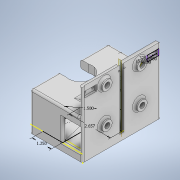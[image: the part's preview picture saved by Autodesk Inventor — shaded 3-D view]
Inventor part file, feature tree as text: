
AUTODESK INVENTOR PART (.ipt)
format: ipt  version: 2020 (Build 240168000, 168)  size: 502,784 bytes
history: native  units: in
note: dims shown in document units (in); Inventor stores cm internally (conversion verified against a paired STEP export)
features: sketch x18, extrude x14, hole x4, plane x1, mirror x1, fillet x1
ambient origin geometry x8: Origin, YZ Plane, XZ Plane, XY Plane, X Axis, Y Axis, Z Axis, Center Point
bodies: Solid1 (feature_tree)
feature tree (39):
  extrude  "Extrusion1"  Depth=5.0299in
  extrude  "Extrusion2"  Depth=0.375in
  extrude  "Extrusion3"  Depth=2.8543in
  sketch  "Sketch5"  dims[d24=5.315in d25=4.5472in]
  extrude  "Extrusion4"  Depth=4.5472in
  extrude  "Extrusion5"  Depth=0.25in
  extrude  "Extrusion6"  Depth=2.6575in
  hole  "Hole2"  [1 undecoded]
  extrude  "Extrusion7"  Depth=0.5in
  extrude  "Extrusion8"  Depth=1.5in
  extrude  "Extrusion9"  Depth=0.5in
  extrude  "Extrusion10"  Depth=0.5in
  hole  "Hole3"  [1 undecoded]
  extrude  "Extrusion11"  Depth=1.5in TaperAngle=0.0deg
  extrude  "Extrusion12"  Depth=1.125in
  hole  "Hole4"  [1 undecoded]
  sketch  "Sketch17"  dims[d63=2.25in d64=90.0deg]
  extrude  "Extrusion13"  TaperAngle=90.0deg  [1 undecoded]
  hole  "Hole5"  [1 undecoded]
  plane  "Work Plane1"
  mirror  "Mirror1"
  extrude  "Extrusion14"  TaperAngle=0.0deg  [1 undecoded]
  fillet  "Fillet1"  Radius=0.625in
  sketch  "Sketch18"  dims[d65=2.25in d66=90.0deg]
  sketch  "Sketch1"  dims[d0=3.3654in d1=5.0299in]
  sketch  "Sketch3"  dims[d3=45.0deg d4=0.375in]
  sketch  "Sketch4"  dims[d5=0.5in d6=0.0in d23=2.8543in]
  sketch  "Sketch6"  dims[d26=0.1in d27=0.0in d28=0.25in]
  sketch  "Sketch7"  dims[d29=0.1in d30=0.0in d31=2.6575in]
  sketch  "Sketch8"  dims[d32=1.5in d33=1.25in]
  sketch  "Sketch9"  dims[d34=1.9685in d35=0.0in d36=0.5in]
  sketch  "Sketch10"  dims[d37=5.03in d38=0.0in d39=1.5in]
  sketch  "Sketch11"  dims[d40=1.0in d41=0.0in d42=0.5in]
  sketch  "Sketch12"  dims[d43=0.0in d44=0.5in]
  sketch  "Sketch13"  dims[d45=0.201in d46=0.75in d47=0.385in d48=0.25in d49=0.5635in d50=1.378in d51=0.0in d52=1.9685in d53=0.0in]
  sketch  "Sketch14"  dims[d54=1.9685in d55=0.0in d56=1.5in d57=0.0in]
  sketch  "Sketch15"  dims[d58=3.75in d59=0.0in d60=1.125in]
  sketch  "Sketch16"  dims[d61=1.49in d62=2.25in]
  sketch  "Sketch19"  dims[d67=0.332in d68=0.375in d69=0.119in d70=0.25in d71=0.5635in d72=0.375in d73=0.0in d74=0.0in d75=0.0in d76=0.625in d77=0.625in d78=0.625in d79=0.625in d80=0.2in d81=0.0in d82=0.21in d83=1.125in d84=0.185in d85=0.37in d86=0.09in d87=0.375in d88=0.119in d89=0.25in d90=0.5635in d91=0.375in d92=0.0in d93=0.375in d94=0.0in d95=0.25in d96=0.5in d97=0.375in d98=0.125in d99=0.0in d100=0.129in d101=0.198in d102=0.225in d103=0.188in d104=0.5635in d105=0.375in d106=0.0in d107=0.125in d108=0.125in d109=1.0in d110=1.0in d111=0.5in d112=1.25in d113=0.0in]
note: 6 required parameter values undecoded (feature->parameter linkage not recoverable at this tier; creation-order binding heuristic only, values carry confidence <= 0.55)
